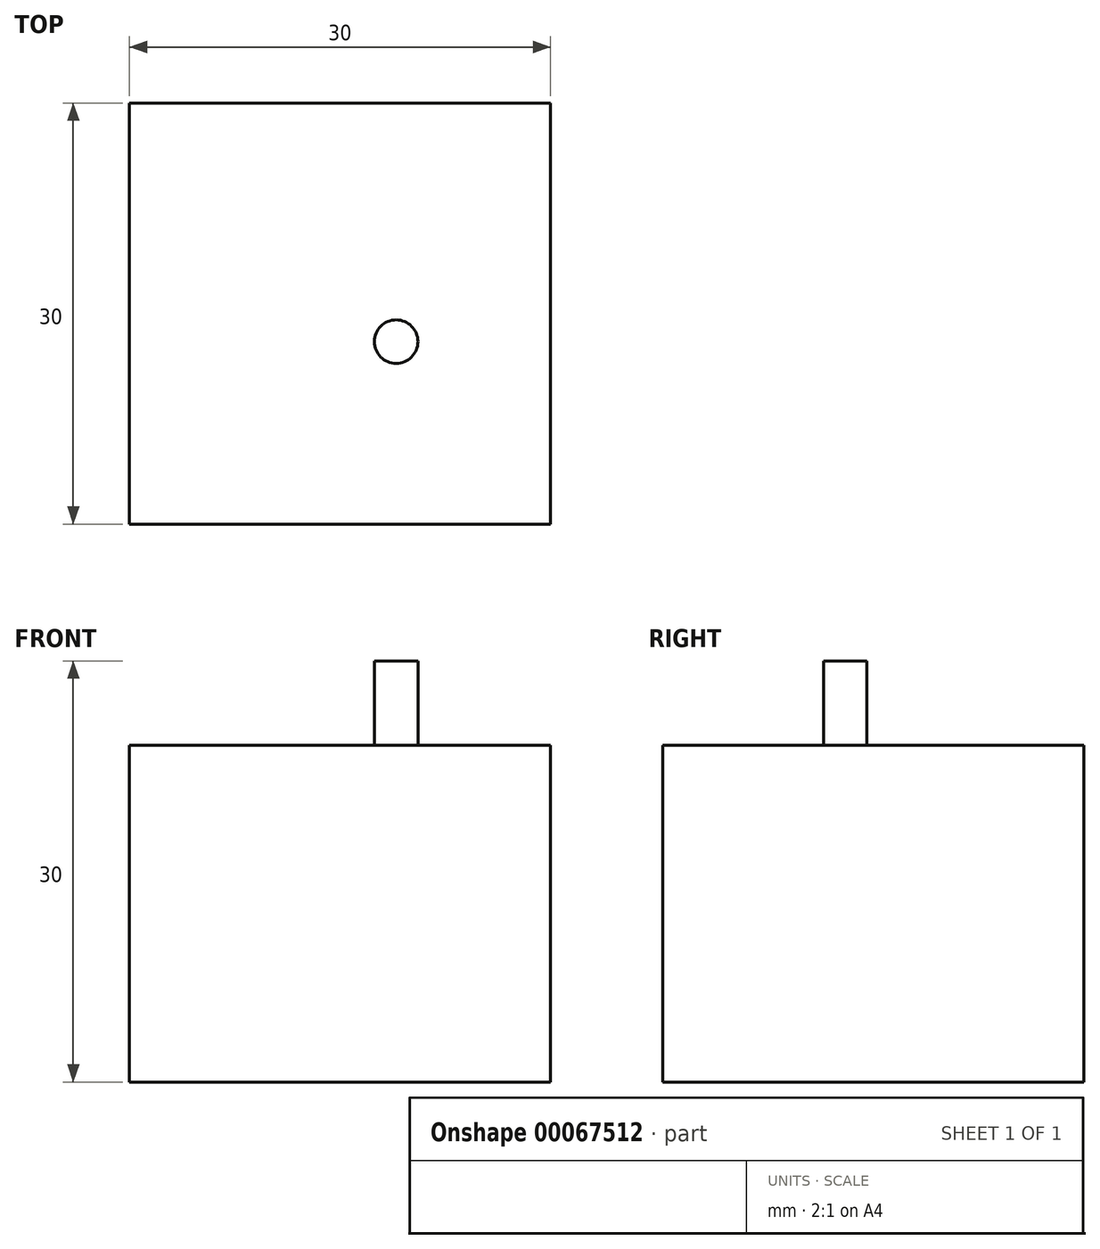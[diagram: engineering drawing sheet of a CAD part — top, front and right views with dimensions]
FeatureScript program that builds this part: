
annotation { "Feature Type Name" : "Feature", "Feature Type Description" : "" }
export const myFeature = defineFeature(function(context is Context, id is Id, definition is map)
    precondition{}
    {
        {
            var Q0;
            Q0=qCreatedBy(makeId("Top.planeOp"),FACE);
            var sketch = newSketch(context, id + "F0", { "sketchPlane" : qUnion([Q0])});
            skLineSegment(sketch, "E0.rect.bottom", {"start": v(15, 15) * mm, "end": v(-15, 15) * mm});
            skLineSegment(sketch, "E0.rect.top", {"start": v(15, -15) * mm, "end": v(-15, -15) * mm});
            skLineSegment(sketch, "E0.rect.left", {"start": v(15, 15) * mm, "end": v(15, -15) * mm});
            skLineSegment(sketch, "E0.rect.right", {"start": v(-15, 15) * mm, "end": v(-15, -15) * mm});
            skPoint(sketch, "E0.rect.middle", {"position": v(0, 0) * mm});
            skSolve(sketch);
        }
        {
            var Q0;
            Q0=qSketchRegion(id+"F0",true);
            extrude(context, id + "F1", {"entities" : qUnion([Q0]), "depth" : 30 * mm});
        }
        {
            var Q0;
            Q0=makeQuery(id+"F1.opExtrude","CAP_FACE",FACE,{"disambiguationData":[OSD([sQuery(id+"F0.wireOp",EDGE,"E0.rect.bottom"),sQuery(id+"F0.wireOp",EDGE,"E0.rect.top"),sQuery(id+"F0.wireOp",EDGE,"E0.rect.left"),sQuery(id+"F0.wireOp",EDGE,"E0.rect.right")])],"isStart":false});
            var sketch = newSketch(context, id + "F2", { "sketchPlane" : qUnion([Q0])});
            skLineSegment(sketch, "E1", {"start": v(0, 0) * mm, "end": v(0, 0) * mm});
            skCircle(sketch, "E2", {"center": v(-4, -2) * mm, "radius": 1.55 * mm});
            skCircle(sketch, "E3.MirrorC", {"center": v(4, -2) * mm, "radius": 1.55 * mm});
            skSolve(sketch);
        }
        {
            var Q0;
            Q0=makeQuery(id+"F2.imprint","IMPRINT",FACE,{"disambiguationData":[TD([[makeQuery(id+"F2.imprint","IMPRINT",EDGE,{"derivedFrom":sQuery(id+"F2.wireOp",EDGE,"6ea1613d-109e-40ce-a016-63cb34eefbe3")}),1.0]])]});
            var Q1;
            Q1=makeQuery(id+"F2.imprint","IMPRINT",FACE,{"disambiguationData":[TD([[makeQuery(id+"F2.imprint","IMPRINT",EDGE,{"derivedFrom":sQuery(id+"F2.wireOp",EDGE,"ea25e9c1-0f7d-4291-a163-112e664b112f0.MirrorC")}),-1.0]])]});
            var Q2;
            Q2=makeQuery(id+"F2.imprint","IMPRINT",FACE,{"disambiguationData":[TD([[makeQuery(id+"F2.imprint","IMPRINT",EDGE,{"derivedFrom":sQuery(id+"F2.wireOp",EDGE,"E3.MirrorC")}),-1.0]])]});
            var Q3;
            Q3=makeQuery(id+"F2.imprint","IMPRINT",FACE,{"disambiguationData":[TD([[makeQuery(id+"F2.imprint","IMPRINT",EDGE,{"derivedFrom":sQuery(id+"F2.wireOp",EDGE,"E2")}),1.0]])]});
            extrude(context, id + "F3", {"entities" : qUnion([Q0, Q1, Q2, Q3]), "operationType" : NewBodyOperationType.REMOVE, "oppositeDirection" : true, "depth" : 6 * mm});
        }
    });
